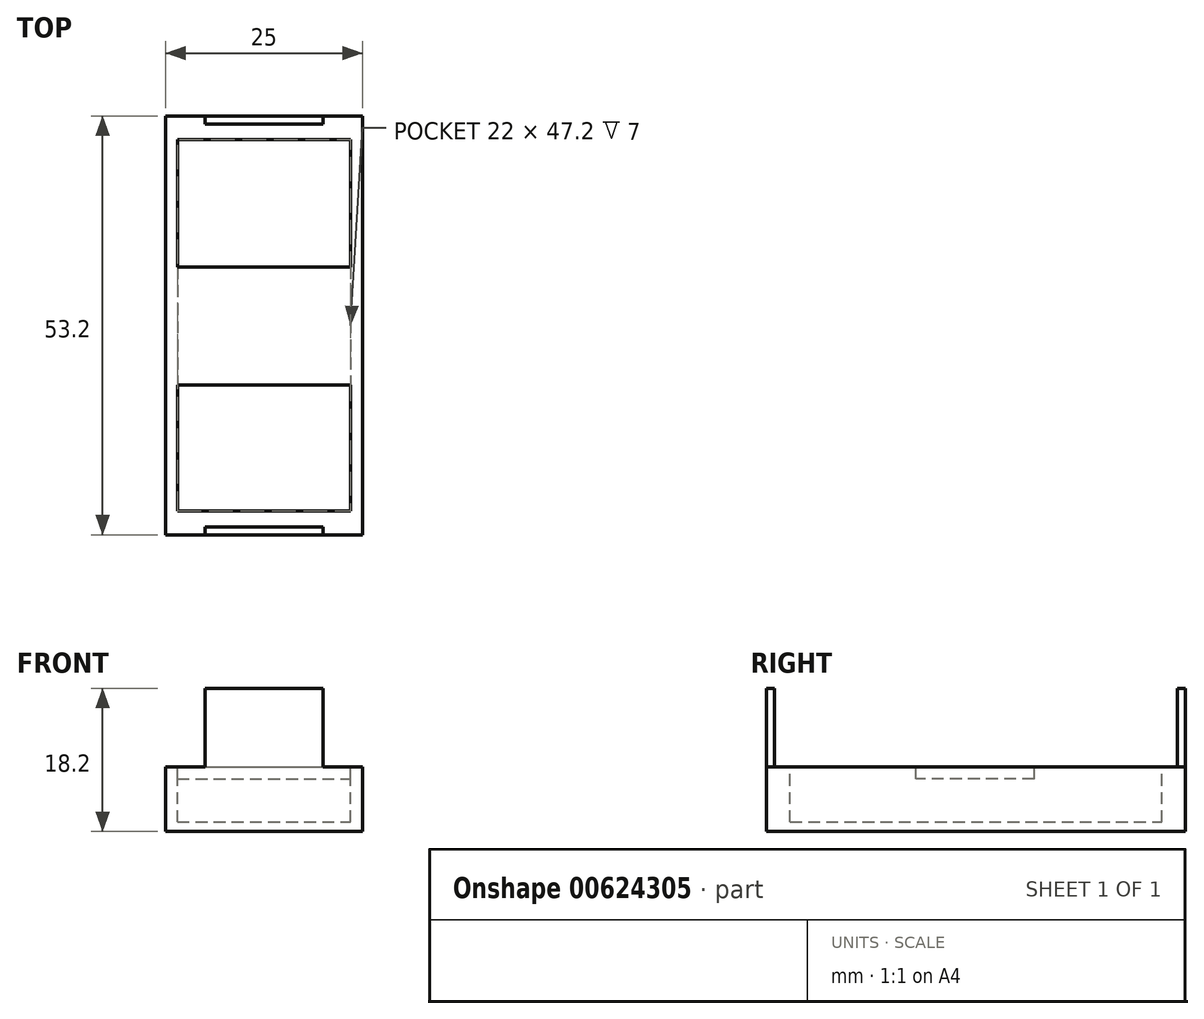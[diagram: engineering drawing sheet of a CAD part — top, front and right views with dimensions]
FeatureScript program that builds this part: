
annotation { "Feature Type Name" : "Feature", "Feature Type Description" : "" }
export const myFeature = defineFeature(function(context is Context, id is Id, definition is map)
    precondition{}
    {
        {
            var Q0;
            Q0=qCreatedBy(makeId("Top.planeOp"),FACE);
            var sketch = newSketch(context, id + "F0", { "sketchPlane" : qUnion([Q0])});
            skLineSegment(sketch, "E0.bottom", {"start": v(0, 0) * mm, "end": v(25, 0) * mm});
            skLineSegment(sketch, "E0.top", {"start": v(0, 53.2) * mm, "end": v(25, 53.2) * mm});
            skLineSegment(sketch, "E0.left", {"start": v(0, 0) * mm, "end": v(0, 53.2) * mm});
            skLineSegment(sketch, "E0.right", {"start": v(25, 0) * mm, "end": v(25, 53.2) * mm});
            skSolve(sketch);
        }
        {
            var Q0;
            Q0 = qSketchRegion(id + "F0", true);
            extrude(context, id + "F1", {"entities" : qUnion([Q0]), "oppositeDirection" : true, "depth" : 8.2 * mm, "offsetDistance" : 25.4 * mm});
        }
        {
            var Q0;
            Q0=qCreatedBy(makeId("Top.planeOp"),FACE);
            var sketch = newSketch(context, id + "F2", { "sketchPlane" : qUnion([Q0])});
            skLineSegment(sketch, "E1.bottom", {"start": v(20, 53.2) * mm, "end": v(5, 53.2) * mm});
            skLineSegment(sketch, "E1.top", {"start": v(20, 52.2) * mm, "end": v(5, 52.2) * mm});
            skLineSegment(sketch, "E1.left", {"start": v(20, 53.2) * mm, "end": v(20, 52.2) * mm});
            skLineSegment(sketch, "E1.right", {"start": v(5, 53.2) * mm, "end": v(5, 52.2) * mm});
            skLineSegment(sketch, "E2.MirrorCS", {"start": v(20, 0) * mm, "end": v(20, 1) * mm});
            skLineSegment(sketch, "E3.MirrorCS", {"start": v(20, 0) * mm, "end": v(5, 0) * mm});
            skLineSegment(sketch, "E4.MirrorCS", {"start": v(20, 1) * mm, "end": v(5, 1) * mm});
            skLineSegment(sketch, "E5.MirrorCS", {"start": v(5, 0) * mm, "end": v(5, 1) * mm});
            skSolve(sketch);
        }
        {
            var Q0;
            Q0 = qSketchRegion(id + "F2", true);
            extrude(context, id + "F3", {"entities" : qUnion([Q0]), "operationType" : NewBodyOperationType.ADD, "depth" : 10 * mm, "offsetDistance" : 25.4 * mm});
        }
        {
            var Q0;
            Q0=qCreatedBy(makeId("Top.planeOp"),FACE);
            var sketch = newSketch(context, id + "F4", { "sketchPlane" : qUnion([Q0])});
            skLineSegment(sketch, "E6.bottom", {"start": v(1.5, 3) * mm, "end": v(23.5, 3) * mm});
            skLineSegment(sketch, "E6.top", {"start": v(1.5, 50.2) * mm, "end": v(23.5, 50.2) * mm});
            skLineSegment(sketch, "E6.left", {"start": v(1.5, 3) * mm, "end": v(1.5, 50.2) * mm});
            skLineSegment(sketch, "E6.right", {"start": v(23.5, 3) * mm, "end": v(23.5, 50.2) * mm});
            skSolve(sketch);
        }
        {
            var Q0;
            Q0 = qSketchRegion(id + "F4", true);
            extrude(context, id + "F5", {"entities" : qUnion([Q0]), "operationType" : NewBodyOperationType.REMOVE, "oppositeDirection" : true, "depth" : 7 * mm, "offsetDistance" : 25.4 * mm});
        }
        {
            var Q0;
            Q0=qCreatedBy(makeId("Top.planeOp"),FACE);
            var sketch = newSketch(context, id + "F6", { "sketchPlane" : qUnion([Q0])});
            skLineSegment(sketch, "E7.bottom", {"start": v(1.5, 34) * mm, "end": v(23.5, 34) * mm});
            skLineSegment(sketch, "E7.top", {"start": v(1.5, 19) * mm, "end": v(23.5, 19) * mm});
            skLineSegment(sketch, "E7.left", {"start": v(1.5, 34) * mm, "end": v(1.5, 19) * mm});
            skLineSegment(sketch, "E7.right", {"start": v(23.5, 34) * mm, "end": v(23.5, 19) * mm});
            skSolve(sketch);
        }
        {
            var Q0;
            Q0 = qSketchRegion(id + "F6", true);
            extrude(context, id + "F7", {"entities" : qUnion([Q0]), "operationType" : NewBodyOperationType.ADD, "oppositeDirection" : true, "depth" : 1.5 * mm, "offsetDistance" : 25.4 * mm});
        }
    });
